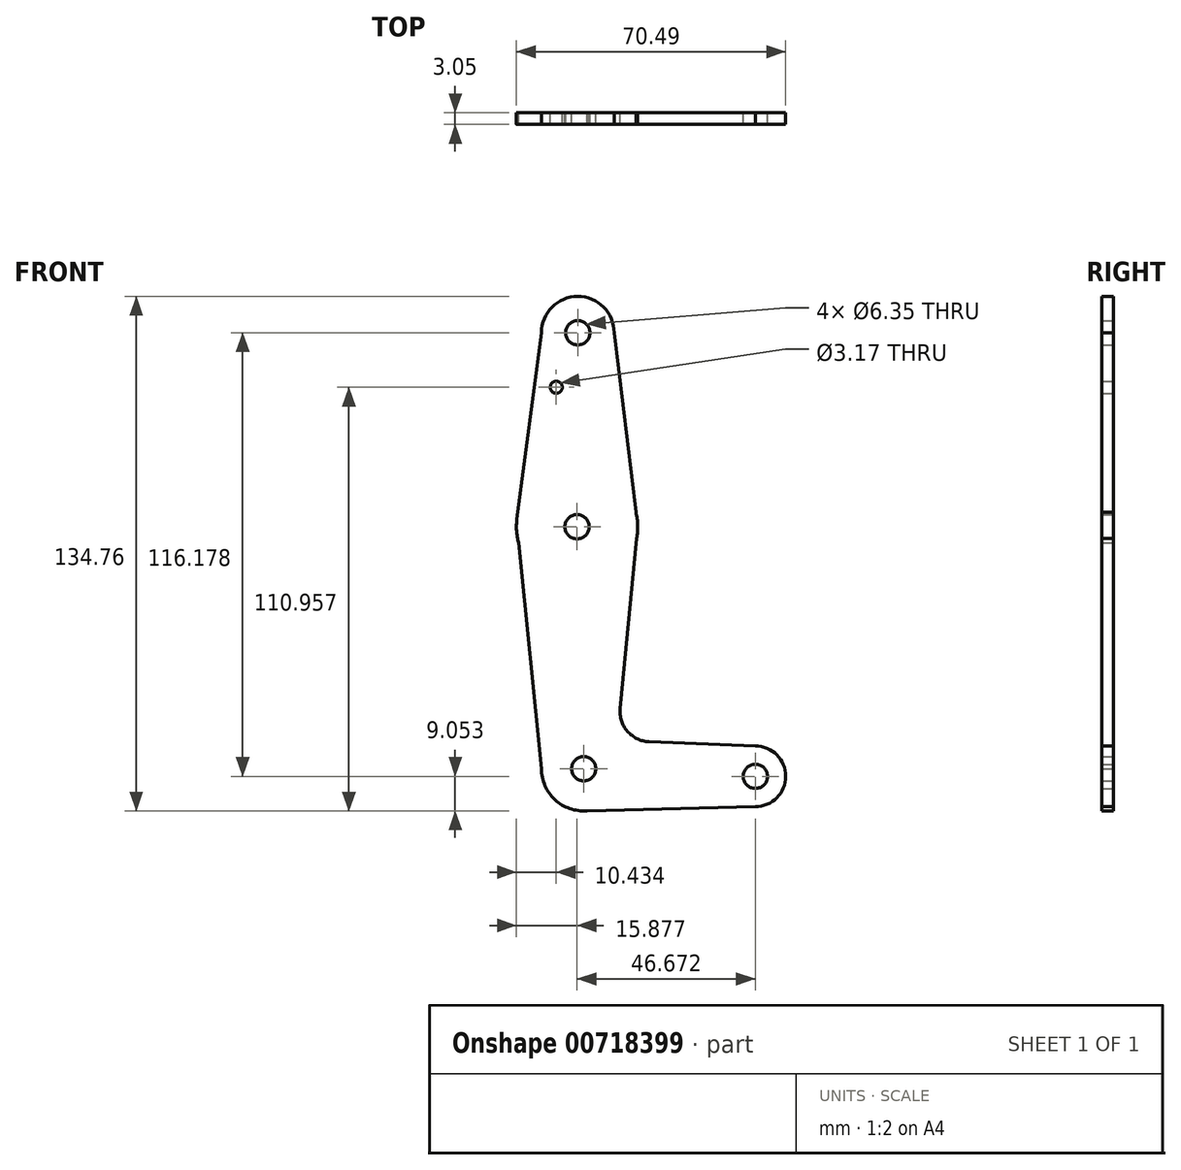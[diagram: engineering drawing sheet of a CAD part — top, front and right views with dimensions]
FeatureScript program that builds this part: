
annotation { "Feature Type Name" : "Feature", "Feature Type Description" : "" }
export const myFeature = defineFeature(function(context is Context, id is Id, definition is map)
    precondition{}
    {
        {
            var Q0;
            Q0=qCreatedBy(makeId("Front.planeOp"),FACE);
            var sketch = newSketch(context, id + "F0", { "sketchPlane" : qUnion([Q0])});
            skCircle(sketch, "E0", {"center": v(42.26, 29) * mm, "radius": 9.53 * mm});
            skLineSegment(sketch, "E1", {"start": v(42.26, 29) * mm, "end": v(42.26, -85.3) * mm, "construction": true});
            skLineSegment(sketch, "E2", {"start": v(42.26, -85.3) * mm, "end": v(86.71, -85.3) * mm, "construction": true});
            skCircle(sketch, "E3", {"center": v(42.08, -21.8) * mm, "radius": 15.88 * mm});
            skLineSegment(sketch, "E4", {"start": v(32.74, 29) * mm, "end": v(26.34, -19.74) * mm});
            skLineSegment(sketch, "E5", {"start": v(51.79, 29) * mm, "end": v(57.95, -21.8) * mm});
            skCircle(sketch, "E6", {"center": v(42.26, 29) * mm, "radius": 3.18 * mm});
            skCircle(sketch, "E7", {"center": v(36.63, 14.72) * mm, "radius": 1.59 * mm});
            skCircle(sketch, "E8", {"center": v(43.81, -85.2) * mm, "radius": 11.05 * mm});
            skCircle(sketch, "E9", {"center": v(43.81, -85.2) * mm, "radius": 3.18 * mm});
            skCircle(sketch, "E10", {"center": v(88.75, -87.19) * mm, "radius": 7.94 * mm});
            skCircle(sketch, "E11", {"center": v(88.75, -87.19) * mm, "radius": 3.18 * mm});
            skLineSegment(sketch, "E12", {"start": v(44.64, -96.21) * mm, "end": v(88.75, -95.12) * mm});
            skLineSegment(sketch, "E13", {"start": v(88.75, -79.25) * mm, "end": v(60.94, -78.12) * mm});
            skLineSegment(sketch, "E14", {"start": v(57.95, -21.8) * mm, "end": v(53.35, -69.4) * mm});
            skLineSegment(sketch, "E15", {"start": v(26.34, -21.8) * mm, "end": v(32.76, -85.2) * mm});
            skCircle(sketch, "E16", {"center": v(42.08, -21.8) * mm, "radius": 3.18 * mm});
            skPoint(sketch, "E17.newPointB", {"position": v(43.81, -77.42) * mm});
            skArc(sketch, "E17.filletArc", {"start": v(53.35, -69.4) * mm, "mid": v(55.27, -75.4) * mm, "end": v(60.94, -78.12) * mm});
            skSolve(sketch);
        }
        {
            var Q0;
            Q0 = qSketchRegion(id + "F0", true);
            extrude(context, id + "F1", {"entities" : qUnion([Q0]), "depth" : 3.05 * mm, "offsetDistance" : 25.4 * mm});
        }
    });
